# Revit family: Scrub Sink-Metcraft-Health Care-9111-1
name_source: partatom
category: Plumbing Fixtures
revit_build: Autodesk Revit MEP 2015 (Build: 20140606_1530(x64)
units: mm (PartAtom-declared; Revit-internal decimal feet)

## types (1)
- Scrub Sink
    ADA Compliant = N.A.
    Assembly Code = D2010430
    CW Connection = Yes
    Description = Single Station Scrub Sink
    Fixture Hyperlink = http://metcraftindustries.com
    Fixture Submittal = http://metcraftindustries.com
    HW Connection = Yes
    Instalation Type = Front Mounted fixture, Wall Outlet Waste
    Lav. C.W. Connection = .5"
    Lav. H.W. Connection = .5"
    Manufacturer = Metcraft Industries
    Manufacturer URL = http://metcraftindustries.com
    MasterFormat Title = Healthcare Plumbing Fixture-Sink
    Masterformat Number = 22 43 16
    Material = 304 Stainless Steel
    Model = 9111-1
    Mounting Height = 3' - 0"
    Omniclass Number = 23-31 13 00
    Omniclass Title = Sinks
    Suggested Faucet = http://www.zurn.com
    Waste Connection = Yes
    Waste Tube = 1.5"

## geometry (parser evidence)
native form markers: Blend x80, Sweep x12
no freeform markers — native parametric forms only
